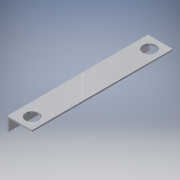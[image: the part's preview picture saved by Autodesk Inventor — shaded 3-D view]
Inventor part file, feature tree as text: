
AUTODESK INVENTOR PART (.ipt)
format: ipt  version: 2016 (Build 200138000, 138)  size: 118,272 bytes
history: native  units: in
note: dims shown in document units (in); Inventor stores cm internally (conversion verified against a paired STEP export)
features: extrude x3, sketch x3
ambient origin geometry x8: Origin, YZ Plane, XZ Plane, XY Plane, X Axis, Y Axis, Z Axis, Center Point
bodies: Solid1 (feature_tree)
feature tree (6):
  extrude  "Extrusion1"  Depth=2.0in
  extrude  "Extrusion2"  Depth=1.0in
  extrude  "Extrusion3"  Depth=1.0in
  sketch  "Sketch1"  dims[d0=12.0in d1=2.0in]
  sketch  "Sketch2"  dims[d2=1.0in d3=1.0in]
  sketch  "Sketch3"  dims[d4=1.0in d5=1.0in d6=1.125in d7=1.125in d8=0.125in d9=0.0in d10=0.125in d11=0.0in d12=1.0in d13=0.0in]
